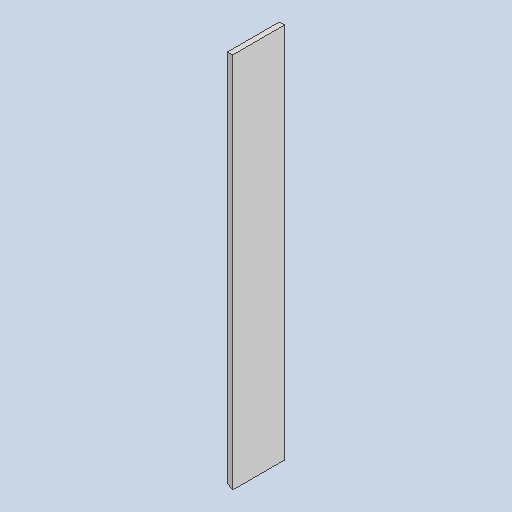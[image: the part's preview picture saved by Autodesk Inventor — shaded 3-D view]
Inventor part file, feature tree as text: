
AUTODESK INVENTOR PART (.ipt)
format: ipt  version: 2025 (Build 290162010, 162A)  size: 94,720 bytes
history: native  units: mm
features: extrude x1, sketch x1
ambient origin geometry x8: Origin, YZ Plane, XZ Plane, XY Plane, X Axis, Y Axis, Z Axis, Center Point
bodies: Solid1 (feature_tree)
feature tree (2):
  extrude  "Extrusion1"  Depth=80.0mm
  sketch  "Sketch1"  dims[d0=513.0mm d1=260.0mm d2=635.0mm d10=5.0mm d11=8.0mm d12=80.0mm d13=0.0mm]
